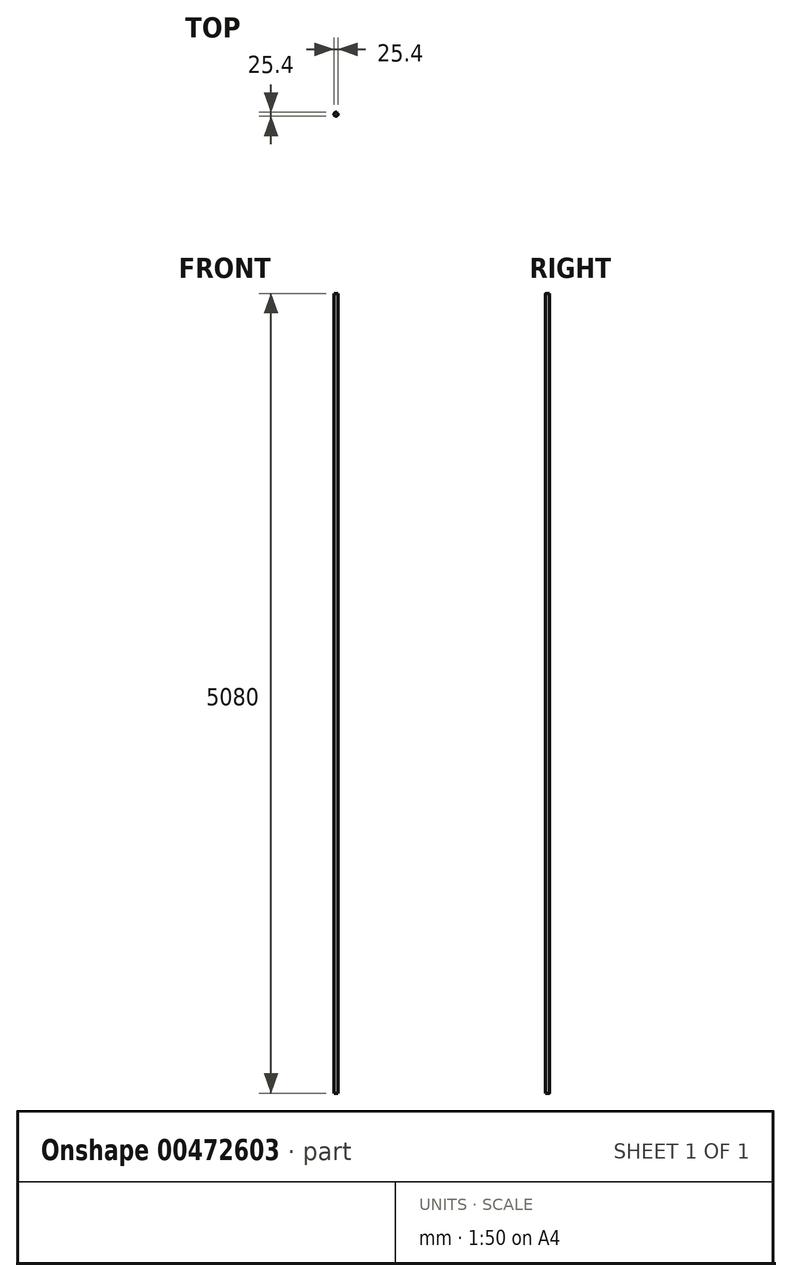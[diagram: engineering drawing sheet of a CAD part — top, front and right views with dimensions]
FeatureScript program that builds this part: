
annotation { "Feature Type Name" : "Feature", "Feature Type Description" : "" }
export const myFeature = defineFeature(function(context is Context, id is Id, definition is map)
    precondition{}
    {
        {
            var Q0;
            Q0=qCreatedBy(makeId("Top.planeOp"),FACE);
            var sketch = newSketch(context, id + "F0", { "sketchPlane" : qUnion([Q0])});
            skCircle(sketch, "E0", {"center": v(0, 0) * mm, "radius": 12.7 * mm});
            skSolve(sketch);
        }
        {
            var Q0;
            Q0=sQuery(id+"F0.wireOp",EDGE,"E0");
            extrude(context, id + "F1", {"bodyType" : ToolBodyType.SURFACE, "surfaceEntities" : qUnion([Q0]), "depth" : 2540 * mm, "hasSecondDirection" : true, "secondDirectionOppositeDirection" : true, "secondDirectionDepth" : 2540 * mm});
        }
    });
